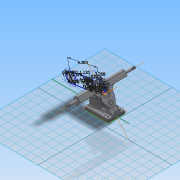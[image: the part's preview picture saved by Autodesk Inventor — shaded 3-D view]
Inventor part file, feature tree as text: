
AUTODESK INVENTOR PART (.ipt)
format: ipt  version: 2014 SP2 (Build 180246200, 246)  size: 476,160 bytes
history: native  units: in
note: dims shown in document units (in); Inventor stores cm internally (conversion verified against a paired STEP export)
features: other x14, sketch x1
ambient origin geometry x8: Origin, YZ Plane, XZ Plane, XY Plane, X Axis, Y Axis, Z Axis, Center Point
bodies: Solid1 (feature_tree), Solid2 (feature_tree), Solid3 (feature_tree)
feature tree (15):
  other  "Truck Caliber50 9in.iam"
  other  "Baseplate Caliber50 9in.ipt:1"
  other  "Hanger Caliber50 9in.ipt:1"
  other  "Generic Riser.ipt:1"
  other  "Axle Centers"
  other  "Parts"
  other  "Work Axis1"
  other  "Work Axis2"
  other  "Work Axis3"
  other  "Vertical Axis"
  other  "Axle Axis"
  other  "Kingpin Axis"
  other  "Work Point1"
  other  "Axle"
  sketch  "Sketch1"  dims[d0=0.3937in d2=3.2677in d3=0.2756in d4=1.9291in d5=4.0625in d9=0.4921in d10=1.5748in d12=360.0deg d14=0.25in d15=0.25in d19=0.1065in d20=0.1065in d21=0.25in d22=0.1065in d23=0.1065in d24=0.25in d25=0.1065in d26=0.1065in d27=0.25in d28=0.1065in d29=0.1065in d30=0.0312in d32=1.378in d34=0.25in d35=0.1875in d36=0.1875in d41=0.1875in d42=0.1875in d49=0.1875in d50=0.1875in d54=0.1875in d55=0.1875in d61=0.25in d64=0.0312in d65=0.25in d66=0.25in d67=0.8in d68=1.626in d69=0.9288in d70=0.355in d71=0.3435in d74=0.4366in d75=0.3033in d76=0.3033in d77=0.6065in d78=0.6065in d79=1.1205in d80=0.3033in d81=0.3033in]
